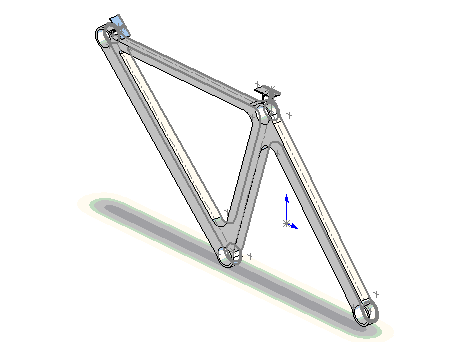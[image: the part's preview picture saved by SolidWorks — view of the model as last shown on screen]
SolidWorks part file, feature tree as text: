
SOLIDWORKS PART (.sldprt)
format: sldprt  version: not decoded by parser v0  size: 614,912 bytes
history: native  units: mm
features: extrude x59, sketch x1 (+11 scaffold rows collapsed)
feature tree (71):
  scaffold x11  (default folders/planes/origin — collapsed)
  sketch  "Sketch1"  dims[c1.D1=10.3124mm c1.D2=12.7mm c1.D3=12.7mm c1.D4=12.7mm c1.D5=12.7mm c1.D8=9.525mm c1.D15=9.525mm c1.D16=6.35mm c2.D8=6.35mm c2.D17=6.35mm c2.D18=6.35mm c2.D19=1.27mm c2.D20=1.27mm c2.D21=1.27mm c2.D28=1.27mm c2.D32=1.27mm c2.D2=~10.111089mm c2.D22=12.7mm c2.D24=~17.603723mm c3.D24=45.0deg c3.D25=0.508mm c3.D27=12.7mm c3.D29=6.35mm c3.D30=6.35mm c3.D31=12.7mm c3.D14=~63.707771mm c3.D19=0.508mm c3.D32=1.27mm c3.D22=12.7mm c4.D32=~1.694056mm c4.D6=4.7625mm c4.D7=4.7625mm c4.D9=4.7625mm c4.D10=4.7625mm c4.D11=~5.55625mm c4.D12=~5.55625mm c4.D13=~2.38125mm c4.D14=~2.38125mm c4.D20=0.254mm c4.D21=0.254mm c4.D23=0.254mm c4.D24=0.254mm c4.D25=0.254mm c4.D26=0.254mm]
  extrude  "Extrude10"  Depth=6.35mm cosMaterialEX=10009317
  extrude  "sMaterialName"  [1 undecoded]
  extrude  "cosFMVItemName"  [1 undecoded]
  extrude  "cosMaterialName"  [1 undecoded]
  extrude  "cosComponentName"  [1 undecoded]
  extrude  "cosMaterialType"  [1 undecoded]
  extrude  "cosMaterialLibFile"  [1 undecoded]
  extrude  "cosMaterialRefPlaneName"  [1 undecoded]
  extrude  "sMaterialSourceName"  [1 undecoded]
  extrude  "sMaterialName"  [1 undecoded]
  extrude  "cosFMVItemName"  [1 undecoded]
  extrude  "cosMaterialName"  [1 undecoded]
  extrude  "cosComponentName"  [1 undecoded]
  extrude  "cosMaterialType"  [1 undecoded]
  extrude  "cosMaterialLibFile"  [1 undecoded]
  extrude  "cosMaterialRefPlaneName"  [1 undecoded]
  extrude  "cosRestraintRefPlaneName"  [1 undecoded]
  extrude  "cosFMVItemName"  [1 undecoded]
  extrude  "cosLBCSymbolColor"  Depth=0 cosRestraint7=0
  extrude  "cosRestraintRefPlaneName"  [1 undecoded]
  extrude  "cosFMVItemName"  [1 undecoded]
  extrude  "cosLBCSymbolColor"  [1 undecoded]
  extrude  "cosRestraintRefPlaneName"  [1 undecoded]
  extrude  "cosFMVItemName"  [1 undecoded]
  extrude  "cosLBCSymbolColor"  [1 undecoded]
  extrude  "cosForceRefPlaneName"  [1 undecoded]
  extrude  "cosFMVItemName"  [1 undecoded]
  extrude  "cosDistributionCoordSysName"  [1 undecoded]
  extrude  "cosLBCSymbolColor"  Depth=0 cosForce7=0
  extrude  "cosForceRefPlaneName"  [1 undecoded]
  extrude  "cosFMVItemName"  [1 undecoded]
  extrude  "cosDistributionCoordSysName"  [1 undecoded]
  extrude  "cosLBCSymbolColor"  [1 undecoded]
  extrude  "cosForceRefPlaneName"  [1 undecoded]
  extrude  "cosFMVItemName"  [1 undecoded]
  extrude  "cosDistributionCoordSysName"  [1 undecoded]
  extrude  "cosLBCSymbolColor"  [1 undecoded]
  extrude  "sMaterialSourceName"  [1 undecoded]
  extrude  "sMaterialName"  [1 undecoded]
  extrude  "cosFMVItemName"  [1 undecoded]
  extrude  "cosMaterialName"  [1 undecoded]
  extrude  "cosComponentName"  [1 undecoded]
  extrude  "cosMaterialType"  [1 undecoded]
  extrude  "cosMaterialLibFile"  [1 undecoded]
  extrude  "cosMaterialRefPlaneName"  [1 undecoded]
  extrude  "cosRestraintRefPlaneName"  [1 undecoded]
  extrude  "cosFMVItemName"  [1 undecoded]
  extrude  "cosLBCSymbolColor"  [1 undecoded]
  extrude  "cosRestraintRefPlaneName"  [1 undecoded]
  extrude  "cosFMVItemName"  [1 undecoded]
  extrude  "cosLBCSymbolColor"  [1 undecoded]
  extrude  "cosForceRefPlaneName"  [1 undecoded]
  extrude  "cosFMVItemName"  [1 undecoded]
  extrude  "cosDistributionCoordSysName"  [1 undecoded]
  extrude  "cosLBCSymbolColor"  [1 undecoded]
  extrude  "cosForceRefPlaneName"  [1 undecoded]
  extrude  "cosFMVItemName"  [1 undecoded]
  extrude  "cosDistributionCoordSysName"  [1 undecoded]
  extrude  "cosLBCSymbolColor"  Depth=0 cosFaceID=0
decode coverage: 5 of 60 modeling features carry decoded parameters
note: ~ marks probable driven/reference dimensions
note: 55 parameter values undecoded
summary: no parameter record found for 55 features
note: suppression state not decoded; provenance and decode notes live in map.json
